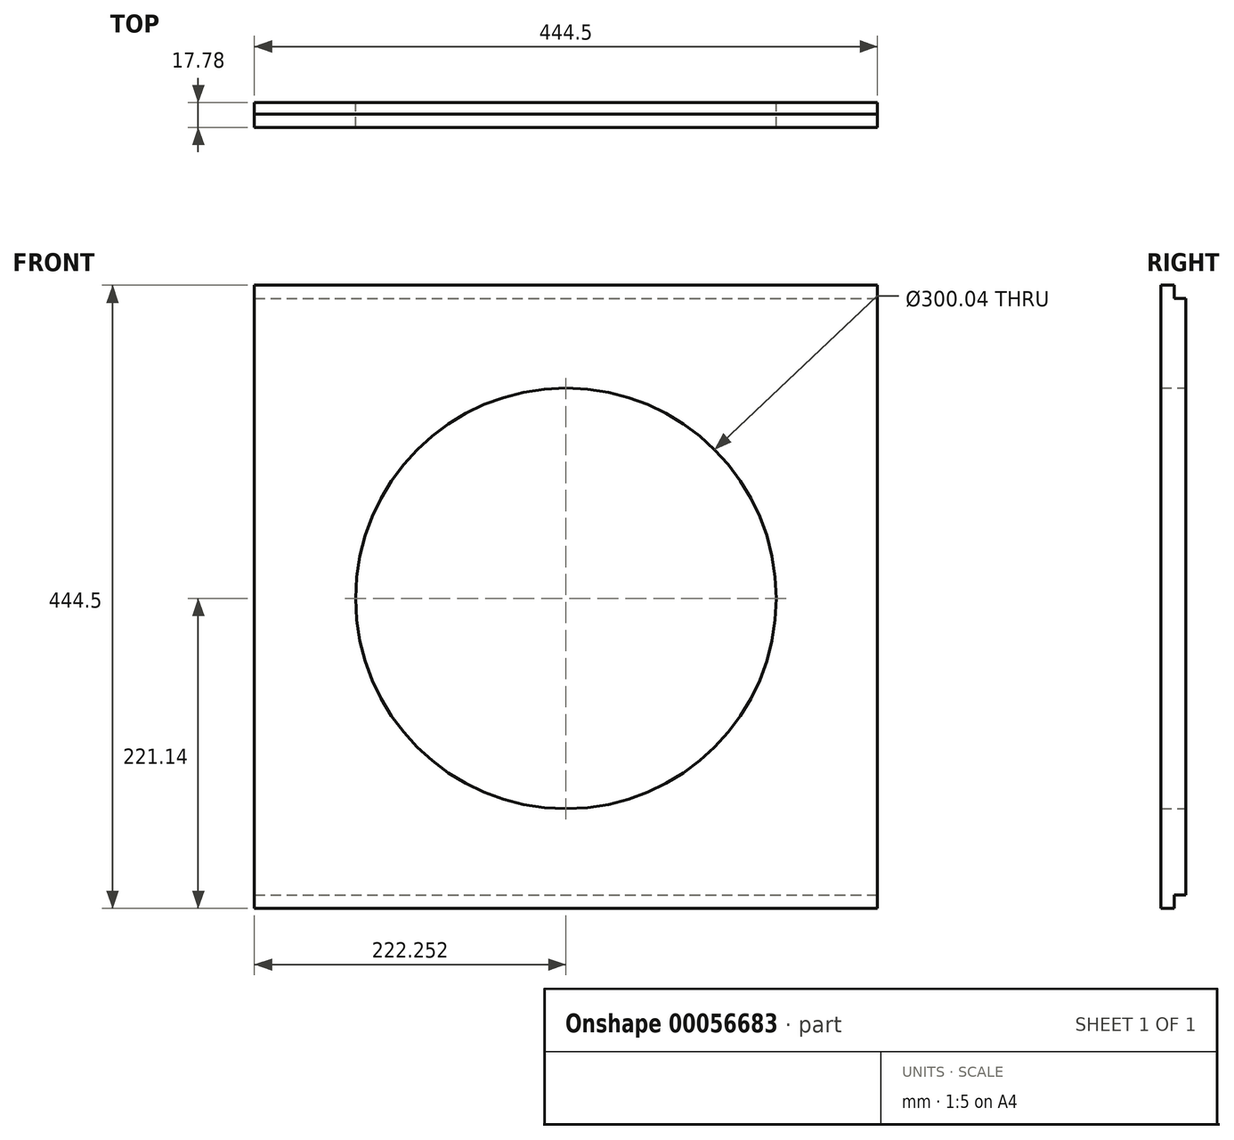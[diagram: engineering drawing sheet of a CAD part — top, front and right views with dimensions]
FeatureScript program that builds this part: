
annotation { "Feature Type Name" : "Feature", "Feature Type Description" : "" }
export const myFeature = defineFeature(function(context is Context, id is Id, definition is map)
    precondition{}
    {
        {
            var Q0;
            Q0=qCreatedBy(makeId("Front.planeOp"),FACE);
            var sketch = newSketch(context, id + "F0", { "sketchPlane" : qUnion([Q0])});
            skLineSegment(sketch, "E0.bottom", {"start": v(-243.06, 223.36) * mm, "end": v(201.44, 223.36) * mm});
            skLineSegment(sketch, "E0.top", {"start": v(-243.06, -221.14) * mm, "end": v(201.44, -221.14) * mm});
            skLineSegment(sketch, "E0.left", {"start": v(-243.06, 223.36) * mm, "end": v(-243.06, -221.14) * mm});
            skLineSegment(sketch, "E0.right", {"start": v(201.44, 223.36) * mm, "end": v(201.44, -221.14) * mm});
            skLineSegment(sketch, "E1.top", {"start": v(188.74, -221.14) * mm, "end": v(182.4, -221.14) * mm});
            skPoint(sketch, "E2", {"position": v(-20.8, -221.14) * mm});
            skPoint(sketch, "E3", {"position": v(-20.8, 223.36) * mm});
            skLineSegment(sketch, "E4", {"start": v(-20.8, 223.36) * mm, "end": v(-20.8, -221.14) * mm});
            skLineSegment(sketch, "E5.MirrorCS", {"start": v(-230.36, -221.14) * mm, "end": v(-224, -221.14) * mm});
            skLineSegment(sketch, "E6", {"start": v(-224, 0) * mm, "end": v(182.4, 0) * mm});
            skCircle(sketch, "E7", {"center": v(-20.8, 0) * mm, "radius": 150.02 * mm});
            skSolve(sketch);
        }
        {
            var Q0;
            Q0 = qSketchRegion(id + "F0", true);
            extrude(context, id + "F1", {"entities" : qUnion([Q0]), "depth" : 17.78 * mm});
        }
        {
            var Q0;
            Q0=makeQuery(id+"F1.opExtrude","SWEPT_FACE",FACE,{"disambiguationData":[OSD([sQuery(id+"F0.wireOp",EDGE,"E0.right")])]});
            var sketch = newSketch(context, id + "F2", { "sketchPlane" : qUnion([Q0])});
            skLineSegment(sketch, "E8.bottom", {"start": v(-8.26, 223.36) * mm, "end": v(0, 223.36) * mm});
            skLineSegment(sketch, "E8.top", {"start": v(-8.26, 213.83) * mm, "end": v(0, 213.83) * mm});
            skLineSegment(sketch, "E8.left", {"start": v(-8.26, 223.36) * mm, "end": v(-8.26, 213.83) * mm});
            skLineSegment(sketch, "E8.right", {"start": v(0, 223.36) * mm, "end": v(0, 213.83) * mm});
            skLineSegment(sketch, "E9.bottom", {"start": v(0, -211.62) * mm, "end": v(-8.26, -211.62) * mm});
            skLineSegment(sketch, "E9.top", {"start": v(0, -221.14) * mm, "end": v(-8.25, -221.14) * mm});
            skLineSegment(sketch, "E9.left", {"start": v(0, -211.62) * mm, "end": v(0, -221.14) * mm});
            skLineSegment(sketch, "E9.right", {"start": v(-8.26, -211.62) * mm, "end": v(-8.25, -221.14) * mm});
            skSolve(sketch);
        }
        {
            var Q0;
            Q0=makeQuery(id+"F2.imprint","IMPRINT",FACE,{"disambiguationData":[TD([[makeQuery(id+"F2.imprint","IMPRINT",EDGE,{"derivedFrom":sQuery(id+"F2.wireOp",EDGE,"E8.bottom")}),-1.0]])]});
            var Q1;
            Q1=makeQuery(id+"F2.imprint","IMPRINT",FACE,{"disambiguationData":[TD([[makeQuery(id+"F2.imprint","IMPRINT",EDGE,{"derivedFrom":sQuery(id+"F2.wireOp",EDGE,"E9.bottom")}),1.0]])]});
            extrude(context, id + "F3", {"entities" : qUnion([Q0, Q1]), "operationType" : NewBodyOperationType.REMOVE, "oppositeDirection" : true, "depth" : 444.5 * mm});
        }
    });
